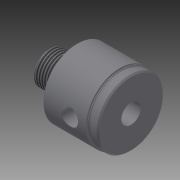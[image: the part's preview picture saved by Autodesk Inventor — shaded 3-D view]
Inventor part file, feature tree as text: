
AUTODESK INVENTOR PART (.ipt)
format: ipt  version: 2014 (Build 180170000, 170)  size: 259,072 bytes
history: native  units: in
note: dims shown in document units (in); Inventor stores cm internally (conversion verified against a paired STEP export)
features: other x112, sketch x5, revolve x4, thread x1, hole x1
ambient origin geometry x8: Origin, YZ Plane, XZ Plane, XY Plane, X Axis, Y Axis, Z Axis, Center Point
bodies: Solid1 (feature_tree)
feature tree (123):
  revolve  "Revolution1"  [1 undecoded]
  thread  "Thread1"  [1 undecoded]
  revolve  "Revolution2"  Angle=360.0deg
  hole  "Hole1"  [1 undecoded]
  revolve  "Revolution3"  [1 undecoded]
  revolve  "Revolution4"  [1 undecoded]
  other  "dp1_XY"
  other  "dp1_YZ"
  other  "dp1_ZX"
  other  "dp1_X"
  other  "dp1_Y"
  other  "dp1_Z"
  other  "dp1_Center"
  other  "dp2_XY"
  other  "dp2_YZ"
  other  "dp2_ZX"
  other  "dp2_X"
  other  "dp2_Y"
  other  "dp2_Z"
  other  "dp2_Center"
  other  "port_XY"
  other  "port_YZ"
  other  "port_ZX"
  other  "port_X"
  other  "port_Y"
  other  "port_Z"
  other  "port_Center"
  other  "rod_guide_XY"
  other  "rod_guide_YZ"
  other  "rod_guide_ZX"
  other  "rod_guide_X"
  other  "rod_guide_Y"
  other  "rod_guide_Z"
  other  "rod_guide_Center"
  other  "s1_XY"
  other  "s1_YZ"
  other  "s1_ZX"
  other  "s1_X"
  other  "s1_Y"
  other  "s1_Z"
  other  "s1_Center"
  other  "s2_XY"
  other  "s2_YZ"
  other  "s2_ZX"
  other  "s2_X"
  other  "s2_Y"
  other  "s2_Z"
  other  "s2_Center"
  other  "t1_XY"
  other  "t1_YZ"
  other  "t1_ZX"
  other  "t1_X"
  other  "t1_Y"
  other  "t1_Z"
  other  "t1_Center"
  other  "t111_XY"
  other  "t111_YZ"
  other  "t111_ZX"
  other  "t111_X"
  other  "t111_Y"
  other  "t111_Z"
  other  "t111_Center"
  other  "to_foot_bracket_XY"
  other  "to_foot_bracket_YZ"
  other  "to_foot_bracket_ZX"
  other  "to_foot_bracket_X"
  other  "to_foot_bracket_Y"
  other  "to_foot_bracket_Z"
  other  "to_foot_bracket_Center"
  other  "to_nut_XY"
  other  "to_nut_YZ"
  other  "to_nut_ZX"
  other  "to_nut_X"
  other  "to_nut_Y"
  other  "to_nut_Z"
  other  "to_nut_Center"
  other  "to_rod_XY"
  other  "to_rod_YZ"
  other  "to_rod_ZX"
  other  "to_rod_X"
  other  "to_rod_Y"
  other  "to_rod_Z"
  other  "to_rod_Center"
  other  "to_screw_XY"
  other  "to_screw_YZ"
  other  "to_screw_ZX"
  other  "to_screw_X"
  other  "to_screw_Y"
  other  "to_screw_Z"
  other  "to_screw_Center"
  other  "to_trunnion_brackets_XY"
  other  "to_trunnion_brackets_YZ"
  other  "to_trunnion_brackets_ZX"
  other  "to_trunnion_brackets_X"
  other  "to_trunnion_brackets_Y"
  other  "to_trunnion_brackets_Z"
  other  "to_trunnion_brackets_Center"
  other  "to_trunnion_brackets1_XY"
  other  "to_trunnion_brackets1_YZ"
  other  "to_trunnion_brackets1_ZX"
  other  "to_trunnion_brackets1_X"
  other  "to_trunnion_brackets1_Y"
  other  "to_trunnion_brackets1_Z"
  other  "to_trunnion_brackets1_Center"
  other  "to_trunnion_brackets2_XY"
  other  "to_trunnion_brackets2_YZ"
  other  "to_trunnion_brackets2_ZX"
  other  "to_trunnion_brackets2_X"
  other  "to_trunnion_brackets2_Y"
  other  "to_trunnion_brackets2_Z"
  other  "to_trunnion_brackets2_Center"
  other  "to_tube_XY"
  other  "to_tube_YZ"
  other  "to_tube_ZX"
  other  "to_tube_X"
  other  "to_tube_Y"
  other  "to_tube_Z"
  other  "to_tube_Center"
  sketch  "Sketch_2"  dims[d0=360.0deg d1=0.3297in d2=0.0in d3=360.0deg]
  sketch  "Sketch_3"  dims[d4=0.442in d5=0.75in d6=0.502in d7=0.25in d8=90.0deg d9=1.875in d10=0.0in d11=360.0deg]
  sketch  "Sketch3"  dims[d12=360.0deg]
  sketch  "Sketch_40"
  sketch  "Sketch_47"
note: 5 required parameter values undecoded (feature->parameter linkage not recoverable at this tier; creation-order binding heuristic only, values carry confidence <= 0.55)